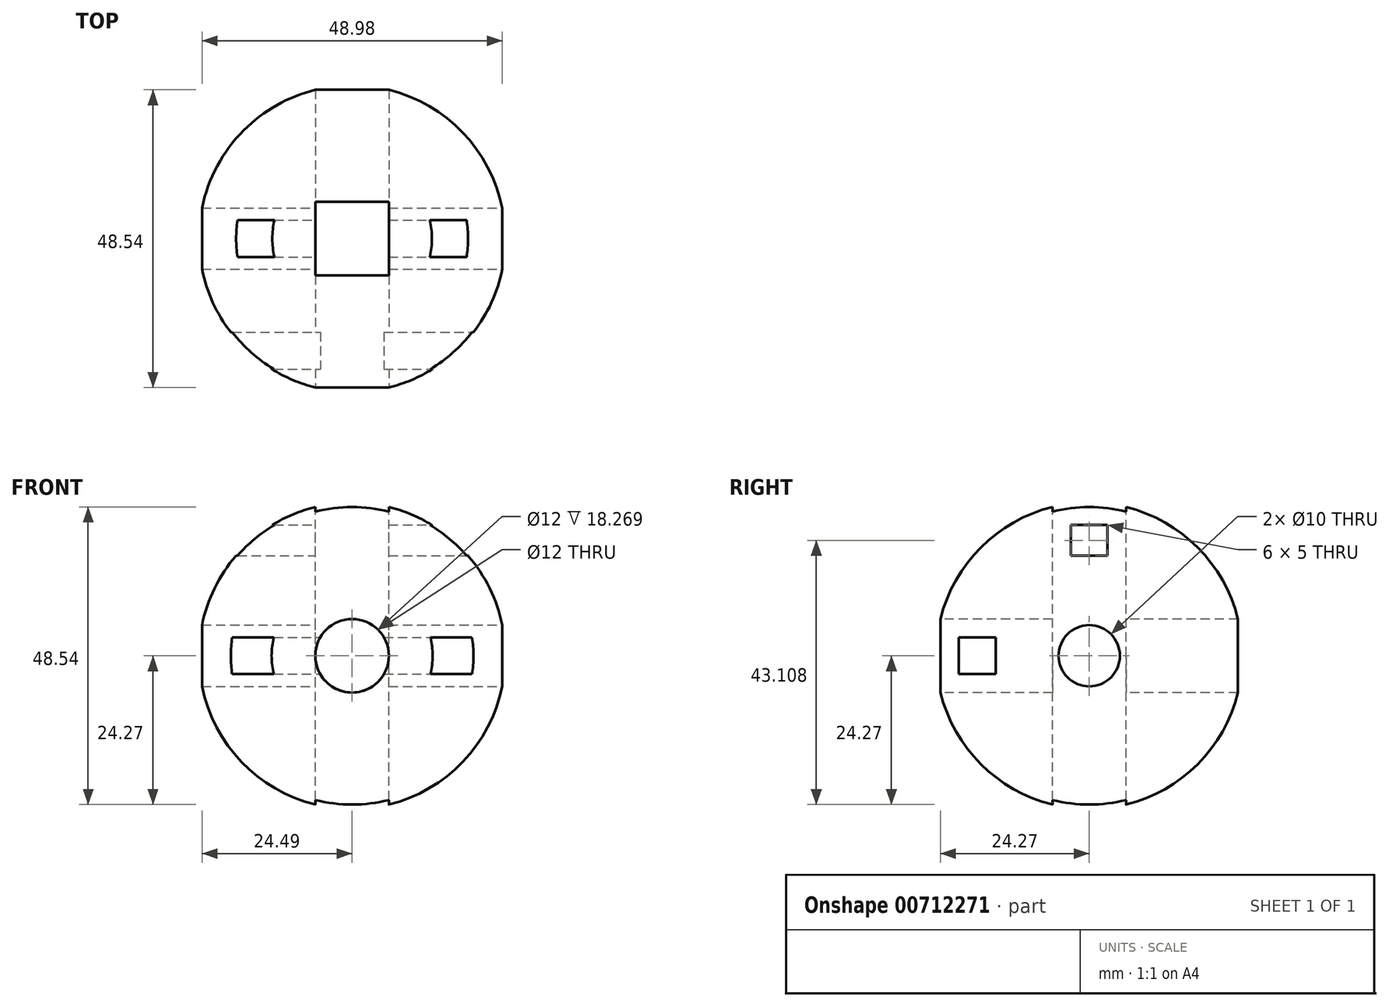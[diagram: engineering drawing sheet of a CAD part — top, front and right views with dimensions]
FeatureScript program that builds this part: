
annotation { "Feature Type Name" : "Feature", "Feature Type Description" : "" }
export const myFeature = defineFeature(function(context is Context, id is Id, definition is map)
    precondition{}
    {
        {
            var Q0;
            Q0=qCreatedBy(makeId("Front.planeOp"),FACE);
            var sketch = newSketch(context, id + "F0", { "sketchPlane" : qUnion([Q0])});
            skCircle(sketch, "E0", {"center": v(0, 0) * mm, "radius": 25 * mm});
            skLineSegment(sketch, "E1", {"start": v(0, 25) * mm, "end": v(0, -25) * mm});
            skSolve(sketch);
        }
        {
            var Q0;
            {var subQ0=sQuery(id+"F0.wireOp",EDGE,"E1");Q0=makeQuery(id+"F0.imprint","IMPRINT",FACE,{"disambiguationData":[TD([[makeQuery(id+"F0.imprint","IMPRINT",EDGE,{"derivedFrom":subQ0}),1.0]])]});}
            var Q1;
            Q1=sQuery(id+"F0.wireOp",EDGE,"E1");
            revolve(context, id + "F1", {"surfaceOperationType" : NewSurfaceOperationType.NEW, "entities" : qUnion([Q0]), "axis" : qUnion([Q1]), "revolveType" : RevolveType.FULL});
        }
        {
            var Q0;
            Q0=qCreatedBy(makeId("Front.planeOp"),FACE);
            cPlane(context, id + "F2", {"entities" : qUnion([Q0]), "cplaneType" : CPlaneType.OFFSET, "offset" : 25 * mm, "width" : 150 * mm, "height" : 150 * mm});
        }
        {
            var Q0;
            Q0=qCreatedBy(id+"F2.planeOp",FACE);
            var sketch = newSketch(context, id + "F3", { "sketchPlane" : qUnion([Q0])});
            skCircle(sketch, "E2", {"center": v(0, 0) * mm, "radius": 6 * mm});
            skSolve(sketch);
        }
        {
            var Q0;
            Q0=makeQuery(id+"F3.imprint","IMPRINT",FACE,{"disambiguationData":[TD([[makeQuery(id+"F3.imprint","IMPRINT",EDGE,{"derivedFrom":sQuery(id+"F3.wireOp",EDGE,"E2")}),1.0]])]});
            extrude(context, id + "F4", {"entities" : qUnion([Q0]), "operationType" : NewBodyOperationType.REMOVE, "endBound" : BoundingType.THROUGH_ALL, "oppositeDirection" : true, "depth" : 25 * mm, "offsetDistance" : 25 * mm});
        }
        {
            var Q0;
            Q0=qCreatedBy(makeId("Top.planeOp"),FACE);
            cPlane(context, id + "F5", {"entities" : qUnion([Q0]), "cplaneType" : CPlaneType.OFFSET, "offset" : 25 * mm, "width" : 150 * mm, "height" : 150 * mm});
        }
        {
            var Q0;
            Q0=qCreatedBy(id+"F5.planeOp",FACE);
            var sketch = newSketch(context, id + "F6", { "sketchPlane" : qUnion([Q0])});
            skLineSegment(sketch, "E3.bottom", {"start": v(6, -6) * mm, "end": v(-6, -6) * mm});
            skLineSegment(sketch, "E3.top", {"start": v(6, 6) * mm, "end": v(-6, 6) * mm});
            skLineSegment(sketch, "E3.left", {"start": v(6, -6) * mm, "end": v(6, 6) * mm});
            skLineSegment(sketch, "E3.right", {"start": v(-6, -6) * mm, "end": v(-6, 6) * mm});
            skPoint(sketch, "E3.middle", {"position": v(0, 0) * mm});
            skSolve(sketch);
        }
        {
            var Q0;
            Q0=makeQuery(id+"F6.imprint","IMPRINT",FACE,{"disambiguationData":[TD([[makeQuery(id+"F6.imprint","IMPRINT",EDGE,{"derivedFrom":sQuery(id+"F6.wireOp",EDGE,"E3.bottom")}),-1.0]])]});
            extrude(context, id + "F7", {"entities" : qUnion([Q0]), "operationType" : NewBodyOperationType.REMOVE, "endBound" : BoundingType.THROUGH_ALL, "oppositeDirection" : true, "depth" : 25 * mm, "offsetDistance" : 25 * mm});
        }
        {
            var Q0;
            Q0=qCreatedBy(makeId("Right.planeOp"),FACE);
            cPlane(context, id + "F8", {"entities" : qUnion([Q0]), "cplaneType" : CPlaneType.OFFSET, "offset" : 25 * mm, "width" : 150 * mm, "height" : 150 * mm});
        }
        {
            var Q0;
            Q0=qCreatedBy(id+"F8.planeOp",FACE);
            var sketch = newSketch(context, id + "F9", { "sketchPlane" : qUnion([Q0])});
            skLineSegment(sketch, "E4.bottom", {"start": v(-3, 16.34) * mm, "end": v(3, 16.34) * mm});
            skLineSegment(sketch, "E4.top", {"start": v(-3, 21.34) * mm, "end": v(3, 21.34) * mm});
            skLineSegment(sketch, "E4.left", {"start": v(-3, 16.34) * mm, "end": v(-3, 21.34) * mm});
            skLineSegment(sketch, "E4.right", {"start": v(3, 16.34) * mm, "end": v(3, 21.34) * mm});
            skPoint(sketch, "E4.middle", {"position": v(0, 18.84) * mm});
            skLineSegment(sketch, "E5.bottom", {"start": v(-15.27, 3) * mm, "end": v(-21.27, 3) * mm});
            skLineSegment(sketch, "E5.top", {"start": v(-15.27, -3) * mm, "end": v(-21.27, -3) * mm});
            skLineSegment(sketch, "E5.left", {"start": v(-15.27, 3) * mm, "end": v(-15.27, -3) * mm});
            skLineSegment(sketch, "E5.right", {"start": v(-21.27, 3) * mm, "end": v(-21.27, -3) * mm});
            skPoint(sketch, "E5.middle", {"position": v(-18.27, 0) * mm});
            skCircle(sketch, "E6", {"center": v(0, 0) * mm, "radius": 5 * mm});
            skSolve(sketch);
        }
        {
            var Q0;
            Q0=makeQuery(id+"F9.imprint","IMPRINT",FACE,{"disambiguationData":[TD([[makeQuery(id+"F9.imprint","IMPRINT",EDGE,{"derivedFrom":sQuery(id+"F9.wireOp",EDGE,"E6")}),1.0]])]});
            var Q1;
            Q1=makeQuery(id+"F9.imprint","IMPRINT",FACE,{"disambiguationData":[TD([[makeQuery(id+"F9.imprint","IMPRINT",EDGE,{"derivedFrom":sQuery(id+"F9.wireOp",EDGE,"E5.bottom")}),1.0]])]});
            var Q2;
            Q2=makeQuery(id+"F9.imprint","IMPRINT",FACE,{"disambiguationData":[TD([[makeQuery(id+"F9.imprint","IMPRINT",EDGE,{"derivedFrom":sQuery(id+"F9.wireOp",EDGE,"E4.bottom")}),1.0]])]});
            extrude(context, id + "F10", {"entities" : qUnion([Q0, Q1, Q2]), "operationType" : NewBodyOperationType.REMOVE, "endBound" : BoundingType.THROUGH_ALL, "oppositeDirection" : true, "depth" : 25 * mm, "offsetDistance" : 25 * mm});
        }
    });
